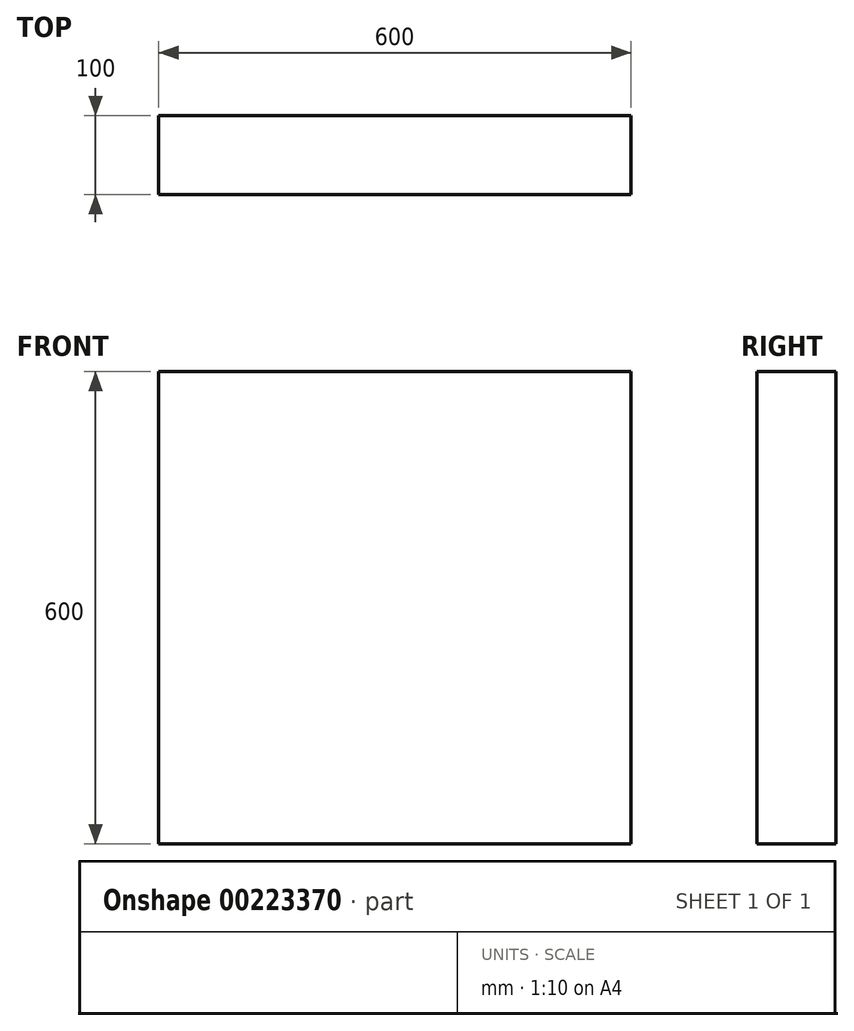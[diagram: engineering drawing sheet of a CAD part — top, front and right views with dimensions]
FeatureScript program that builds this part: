
annotation { "Feature Type Name" : "Feature", "Feature Type Description" : "" }
export const myFeature = defineFeature(function(context is Context, id is Id, definition is map)
    precondition{}
    {
        {
            var Q0;
            Q0=qCreatedBy(makeId("Front.planeOp"),FACE);
            var sketch = newSketch(context, id + "F0", { "sketchPlane" : qUnion([Q0])});
            skLineSegment(sketch, "E0.bottom", {"start": v(300, -300) * mm, "end": v(-300, -300) * mm});
            skLineSegment(sketch, "E0.top", {"start": v(300, 300) * mm, "end": v(-300, 300) * mm});
            skLineSegment(sketch, "E0.left", {"start": v(300, -300) * mm, "end": v(300, 300) * mm});
            skLineSegment(sketch, "E0.right", {"start": v(-300, -300) * mm, "end": v(-300, 300) * mm});
            skPoint(sketch, "E0.middle", {"position": v(0, 0) * mm});
            skSolve(sketch);
        }
        {
            var Q0;
            Q0=makeQuery(id+"F0.imprint","IMPRINT",FACE,{"disambiguationData":[TD([[makeQuery(id+"F0.imprint","IMPRINT",EDGE,{"derivedFrom":sQuery(id+"F0.wireOp",EDGE,"E0.bottom")}),-1.0]])]});
            extrude(context, id + "F1", {"entities" : qUnion([Q0]), "depth" : 100 * mm});
        }
    });
